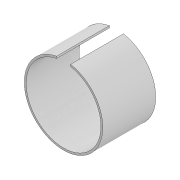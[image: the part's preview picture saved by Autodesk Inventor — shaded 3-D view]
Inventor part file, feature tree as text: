
AUTODESK INVENTOR PART (.ipt)
format: ipt  version: 2020 (Build 240168000, 168)  size: 91,136 bytes
history: native  units: mm
features: other x1, extrude x1, sketch x1
ambient origin geometry x8: Origin, YZ Plane, XZ Plane, XY Plane, X Axis, Y Axis, Z Axis, Center Point
bodies: Body1 (feature_tree)
feature tree (3):
  other  "솔리드1"
  extrude  "돌출1"  Depth=42.4mm
  sketch  "스케치1"
